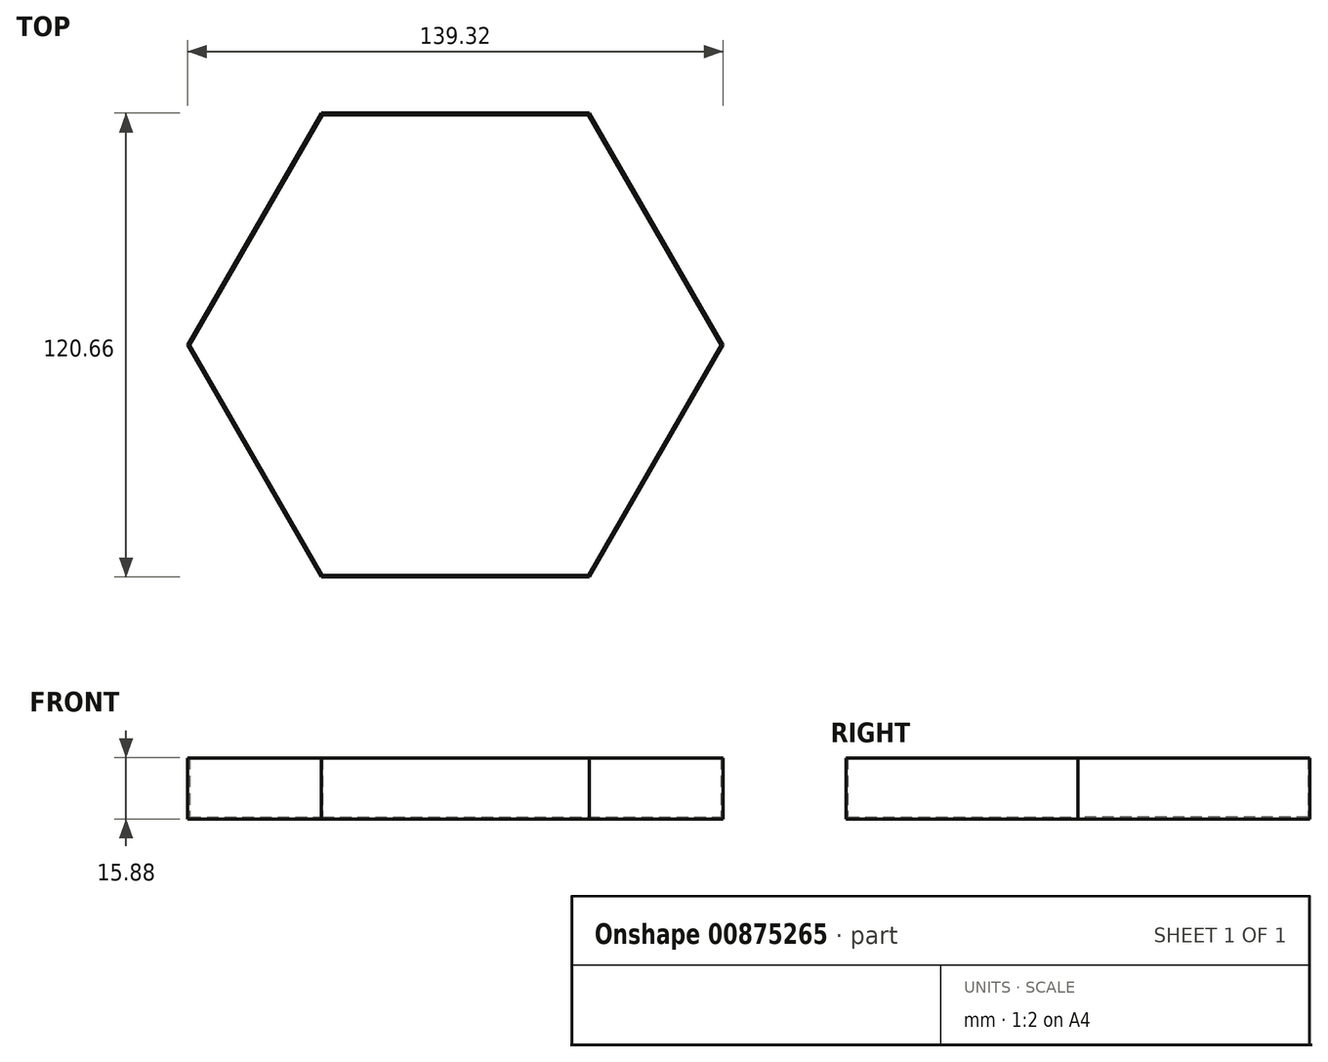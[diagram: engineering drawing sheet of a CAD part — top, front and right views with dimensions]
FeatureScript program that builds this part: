
annotation { "Feature Type Name" : "Feature", "Feature Type Description" : "" }
export const myFeature = defineFeature(function(context is Context, id is Id, definition is map)
    precondition{}
    {
        {
            var Q0;
            Q0=qCreatedBy(makeId("Top.planeOp"),FACE);
            var sketch = newSketch(context, id + "F0", { "sketchPlane" : qUnion([Q0])});
            skCircle(sketch, "E0.cCircle", {"center": v(0, 0) * mm, "radius": 60.33 * mm, "construction": true});
            skLineSegment(sketch, "E0.0", {"start": v(34.83, 60.33) * mm, "end": v(69.66, 0) * mm});
            skLineSegment(sketch, "E0.1", {"start": v(69.66, 0) * mm, "end": v(34.83, -60.33) * mm});
            skLineSegment(sketch, "E0.2", {"start": v(34.83, -60.33) * mm, "end": v(-34.83, -60.33) * mm});
            skLineSegment(sketch, "E0.3", {"start": v(-34.83, -60.33) * mm, "end": v(-69.66, 0) * mm});
            skLineSegment(sketch, "E0.4", {"start": v(-69.66, 0) * mm, "end": v(-34.83, 60.33) * mm});
            skLineSegment(sketch, "E0.5", {"start": v(-34.83, 60.33) * mm, "end": v(34.83, 60.33) * mm});
            skPoint(sketch, "E0.0.midPoint", {"position": v(52.24, 30.16) * mm});
            skSolve(sketch);
        }
        {
            var Q0;
            Q0 = qSketchRegion(id + "F0", true);
            extrude(context, id + "F1", {"entities" : qUnion([Q0]), "depth" : 15.88 * mm, "offsetDistance" : 25.4 * mm});
        }
        {
            var Q0;
            Q0=makeQuery(id+"F1.opExtrude","CAP_FACE",FACE,{"disambiguationData":[OSD([sQuery(id+"F0.wireOp",EDGE,"E0.0"),sQuery(id+"F0.wireOp",EDGE,"E0.1"),sQuery(id+"F0.wireOp",EDGE,"E0.2"),sQuery(id+"F0.wireOp",EDGE,"E0.3"),sQuery(id+"F0.wireOp",EDGE,"E0.4"),sQuery(id+"F0.wireOp",EDGE,"E0.5")])],"isStart":false});
            shell(context, id + "F2", {"entities" : qUnion([Q0]), "thickness" : .4 * mm});
        }
    });
